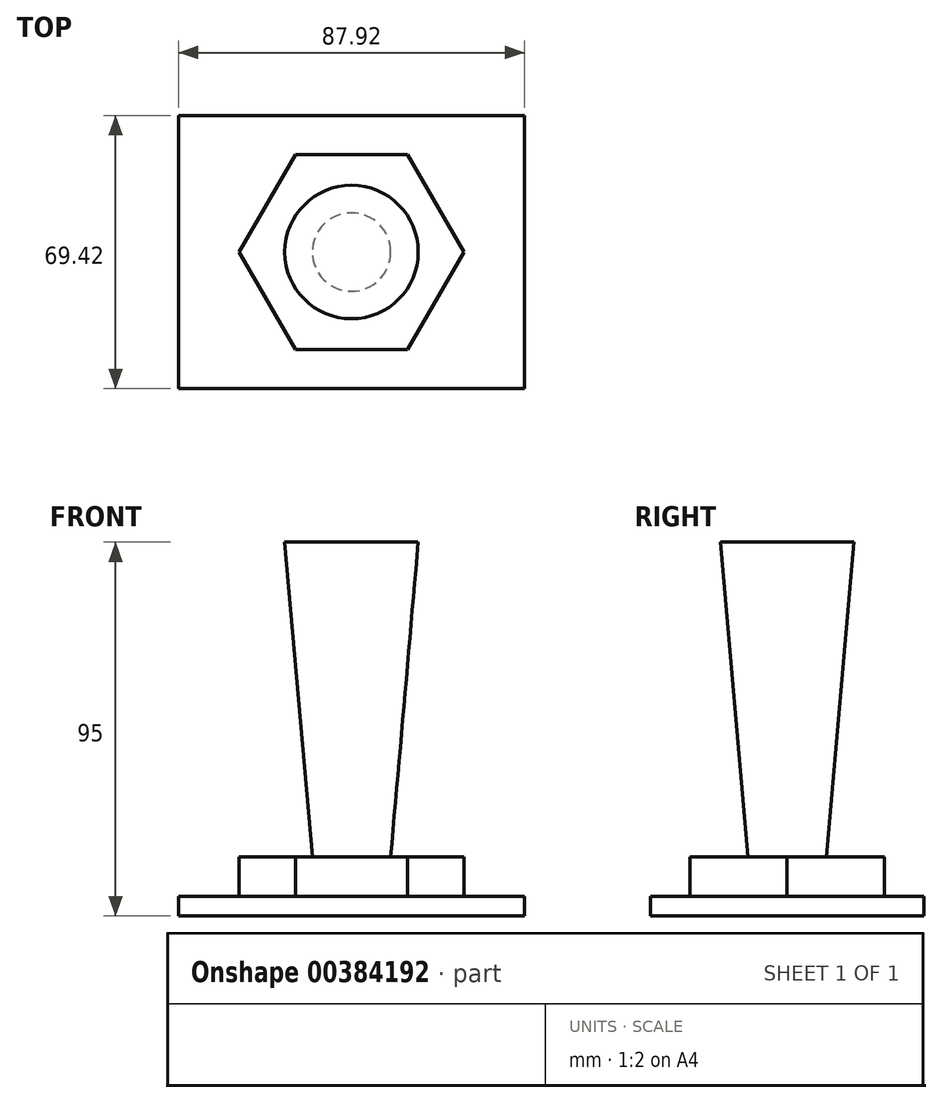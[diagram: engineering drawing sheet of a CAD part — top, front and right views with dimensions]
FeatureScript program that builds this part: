
annotation { "Feature Type Name" : "Feature", "Feature Type Description" : "" }
export const myFeature = defineFeature(function(context is Context, id is Id, definition is map)
    precondition{}
    {
        {
            var Q0;
            Q0=qCreatedBy(makeId("Top.planeOp"),FACE);
            var sketch = newSketch(context, id + "F0", { "sketchPlane" : qUnion([Q0])});
            skLineSegment(sketch, "E0.bottom", {"start": v(43.96, 34.71) * mm, "end": v(-43.96, 34.71) * mm});
            skLineSegment(sketch, "E0.top", {"start": v(43.96, -34.71) * mm, "end": v(-43.96, -34.71) * mm});
            skLineSegment(sketch, "E0.left", {"start": v(43.96, 34.71) * mm, "end": v(43.96, -34.71) * mm});
            skLineSegment(sketch, "E0.right", {"start": v(-43.96, 34.71) * mm, "end": v(-43.96, -34.71) * mm});
            skPoint(sketch, "E0.middle", {"position": v(0, 0) * mm});
            skSolve(sketch);
        }
        {
            var Q0;
            Q0 = qSketchRegion(id + "F0", true);
            extrude(context, id + "F1", {"entities" : qUnion([Q0]), "depth" : 5 * mm});
        }
        {
            var Q0;
            Q0=makeQuery(id+"F1.opExtrude","CAP_FACE",FACE,{"disambiguationData":[OSD([sQuery(id+"F0.wireOp",EDGE,"E0.bottom"),sQuery(id+"F0.wireOp",EDGE,"E0.top"),sQuery(id+"F0.wireOp",EDGE,"E0.left"),sQuery(id+"F0.wireOp",EDGE,"E0.right")])],"isStart":false});
            var sketch = newSketch(context, id + "F2", { "sketchPlane" : qUnion([Q0])});
            skCircle(sketch, "E1.cCircle", {"center": v(0, 0) * mm, "radius": 24.71 * mm, "construction": true});
            skLineSegment(sketch, "E1.0", {"start": v(-14.27, 24.71) * mm, "end": v(14.27, 24.71) * mm});
            skLineSegment(sketch, "E1.1", {"start": v(14.27, 24.71) * mm, "end": v(28.53, 0) * mm});
            skLineSegment(sketch, "E1.2", {"start": v(28.53, 0) * mm, "end": v(14.27, -24.71) * mm});
            skLineSegment(sketch, "E1.3", {"start": v(14.27, -24.71) * mm, "end": v(-14.27, -24.71) * mm});
            skLineSegment(sketch, "E1.4", {"start": v(-14.27, -24.71) * mm, "end": v(-28.53, 0) * mm});
            skLineSegment(sketch, "E1.5", {"start": v(-28.53, 0) * mm, "end": v(-14.27, 24.71) * mm});
            skPoint(sketch, "E1.0.midPoint", {"position": v(0, 24.71) * mm});
            skSolve(sketch);
        }
        {
            var Q0;
            Q0=makeQuery(id+"F2.imprint","IMPRINT",FACE,{"disambiguationData":[TD([[makeQuery(id+"F2.imprint","IMPRINT",EDGE,{"derivedFrom":sQuery(id+"F2.wireOp",EDGE,"E1.0")}),-1.0]])]});
            extrude(context, id + "F3", {"entities" : qUnion([Q0]), "operationType" : NewBodyOperationType.ADD, "depth" : 10 * mm});
        }
        {
            var Q0;
            Q0=makeQuery(id+"F3.opExtrude","CAP_FACE",FACE,{"disambiguationData":[OSD([sQuery(id+"F2.wireOp",EDGE,"E1.0"),sQuery(id+"F2.wireOp",EDGE,"E1.1"),sQuery(id+"F2.wireOp",EDGE,"E1.2"),sQuery(id+"F2.wireOp",EDGE,"E1.3"),sQuery(id+"F2.wireOp",EDGE,"E1.4"),sQuery(id+"F2.wireOp",EDGE,"E1.5")])],"isStart":false});
            var sketch = newSketch(context, id + "F4", { "sketchPlane" : qUnion([Q0])});
            skCircle(sketch, "E2", {"center": v(0, 0) * mm, "radius": 9.96 * mm});
            skSolve(sketch);
        }
        {
            var Q0;
            Q0=makeQuery(id+"F4.imprint","IMPRINT",FACE,{"disambiguationData":[TD([[makeQuery(id+"F4.imprint","IMPRINT",EDGE,{"derivedFrom":sQuery(id+"F4.wireOp",EDGE,"E2")}),1.0]])]});
            extrude(context, id + "F5", {"entities" : qUnion([Q0]), "operationType" : NewBodyOperationType.ADD, "depth" : 80 * mm, "offsetDistance" : 25 * mm, "hasDraft" : true, "draftAngle" : 5 * degree});
        }
    });
